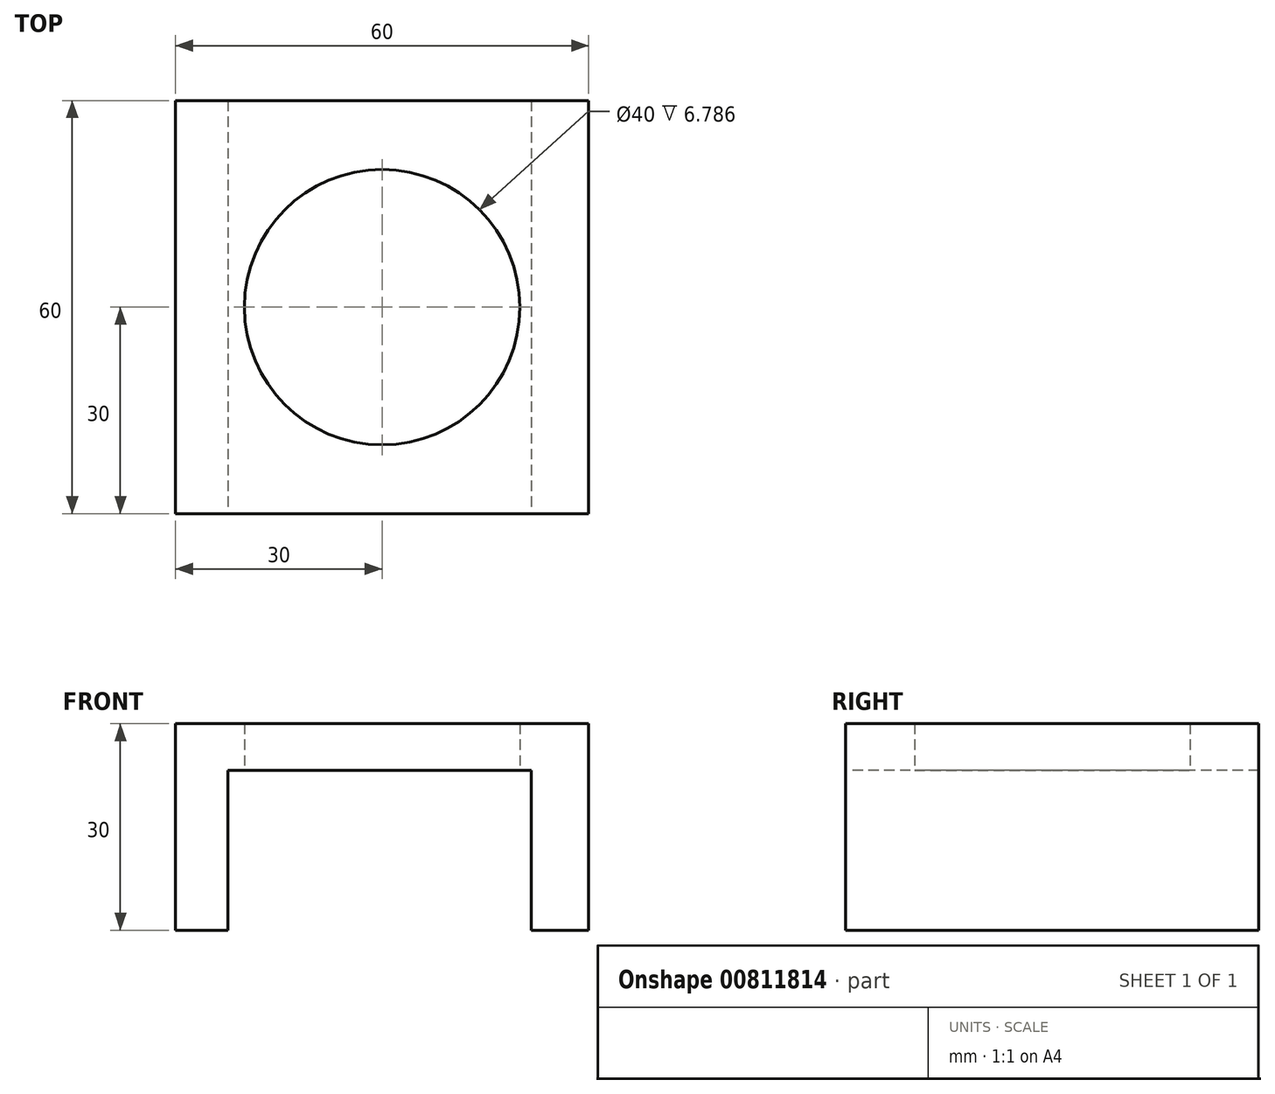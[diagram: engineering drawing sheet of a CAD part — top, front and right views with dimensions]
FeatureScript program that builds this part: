
annotation { "Feature Type Name" : "Feature", "Feature Type Description" : "" }
export const myFeature = defineFeature(function(context is Context, id is Id, definition is map)
    precondition{}
    {
        {
            var Q0;
            Q0=qCreatedBy(makeId("Top.planeOp"),FACE);
            var sketch = newSketch(context, id + "F0", { "sketchPlane" : qUnion([Q0])});
            skCircle(sketch, "E0", {"center": v(0, 0) * mm, "radius": 20 * mm});
            skLineSegment(sketch, "E1.bottom", {"start": v(30, -30) * mm, "end": v(-30, -30) * mm});
            skLineSegment(sketch, "E1.top", {"start": v(30, 30) * mm, "end": v(-30, 30) * mm});
            skLineSegment(sketch, "E1.left", {"start": v(30, -30) * mm, "end": v(30, 30) * mm});
            skLineSegment(sketch, "E1.right", {"start": v(-30, -30) * mm, "end": v(-30, 30) * mm});
            skSolve(sketch);
        }
        {
            var Q0;
            Q0=makeQuery(id+"F0.imprint","IMPRINT",FACE,{"disambiguationData":[TD([[makeQuery(id+"F0.imprint","IMPRINT",EDGE,{"derivedFrom":sQuery(id+"F0.wireOp",EDGE,"E0")}),-1.0]])]});
            extrude(context, id + "F1", {"entities" : qUnion([Q0]), "depth" : 30 * mm, "offsetDistance" : 25.4 * mm});
        }
        {
            var Q0;
            Q0=makeQuery(id+"F1.opExtrude","SWEPT_FACE",FACE,{"disambiguationData":[OSD([sQuery(id+"F0.wireOp",EDGE,"E1.bottom")])]});
            var sketch = newSketch(context, id + "F2", { "sketchPlane" : qUnion([Q0])});
            skLineSegment(sketch, "E2.bottom", {"start": v(-22.44, 23.21) * mm, "end": v(21.68, 23.21) * mm});
            skLineSegment(sketch, "E2.top", {"start": v(-22.44, 0) * mm, "end": v(21.68, 0) * mm});
            skLineSegment(sketch, "E2.left", {"start": v(-22.44, 23.21) * mm, "end": v(-22.44, 0) * mm});
            skLineSegment(sketch, "E2.right", {"start": v(21.68, 23.21) * mm, "end": v(21.68, 0) * mm});
            skSolve(sketch);
        }
        {
            var Q0;
            Q0=makeQuery(id+"F2.imprint","IMPRINT",FACE,{"disambiguationData":[TD([[makeQuery(id+"F2.imprint","IMPRINT",EDGE,{"derivedFrom":sQuery(id+"F2.wireOp",EDGE,"E2.bottom")}),-1.0]])]});
            extrude(context, id + "F3", {"entities" : qUnion([Q0]), "operationType" : NewBodyOperationType.REMOVE, "oppositeDirection" : true, "depth" : 76.2 * mm, "offsetDistance" : 25.4 * mm});
        }
    });
